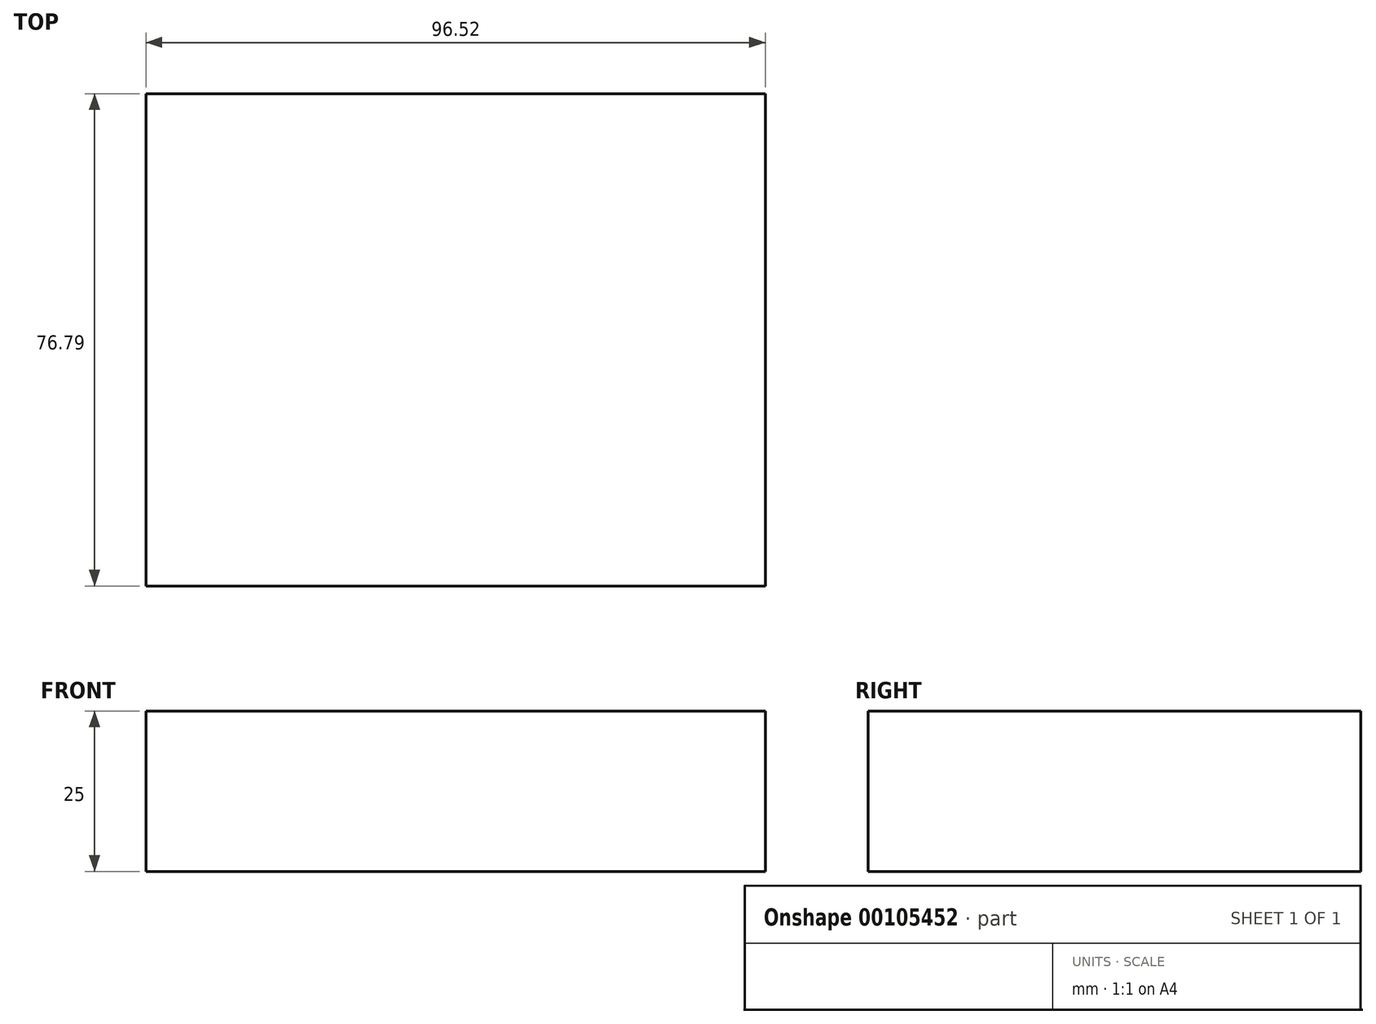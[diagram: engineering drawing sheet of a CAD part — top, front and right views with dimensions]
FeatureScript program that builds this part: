
annotation { "Feature Type Name" : "Feature", "Feature Type Description" : "" }
export const myFeature = defineFeature(function(context is Context, id is Id, definition is map)
    precondition{}
    {
        {
            var Q0;
            Q0=qCreatedBy(makeId("Top.planeOp"),FACE);
            var sketch = newSketch(context, id + "F0", { "sketchPlane" : qUnion([Q0])});
            skLineSegment(sketch, "E0.bottom", {"start": v(-53.55, -41.8) * mm, "end": v(42.97, -41.8) * mm});
            skLineSegment(sketch, "E0.top", {"start": v(-53.55, 34.98) * mm, "end": v(42.97, 34.98) * mm});
            skLineSegment(sketch, "E0.left", {"start": v(-53.55, -41.8) * mm, "end": v(-53.55, 34.98) * mm});
            skLineSegment(sketch, "E0.right", {"start": v(42.97, -41.8) * mm, "end": v(42.97, 34.98) * mm});
            skSolve(sketch);
        }
        {
            var Q0;
            Q0=makeQuery(id+"F0.imprint","IMPRINT",FACE,{"disambiguationData":[TD([[makeQuery(id+"F0.imprint","IMPRINT",EDGE,{"derivedFrom":sQuery(id+"F0.wireOp",EDGE,"E0.bottom")}),1.0]])]});
            extrude(context, id + "F1", {"entities" : qUnion([Q0]), "depth" : 25 * mm});
        }
    });
